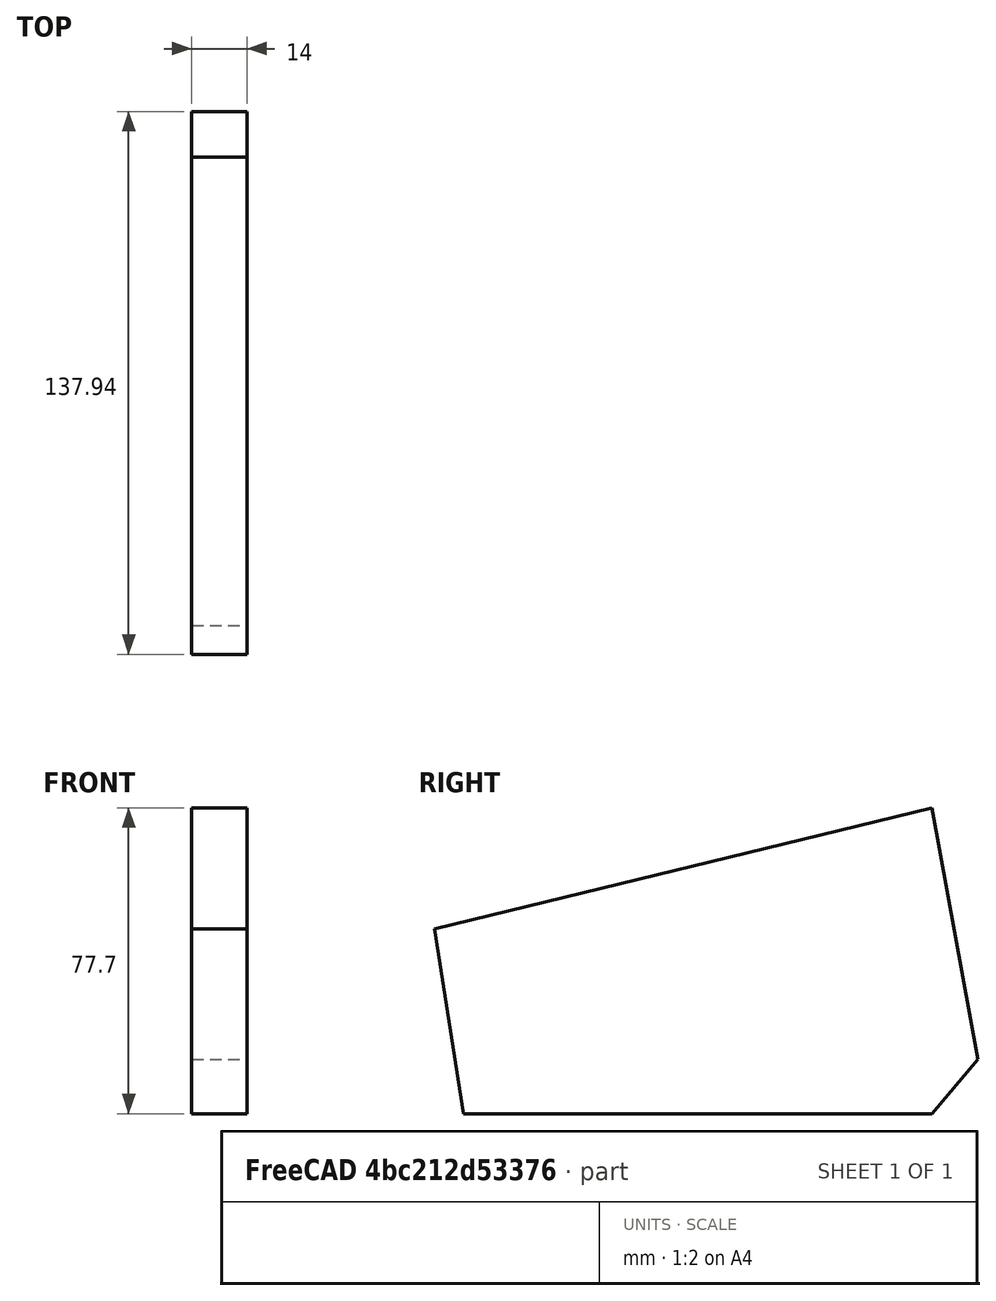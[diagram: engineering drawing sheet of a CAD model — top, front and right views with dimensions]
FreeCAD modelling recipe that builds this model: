
FCSTD DOCUMENT  (FreeCAD 1.0R39109 (Git))
Label: Griffschale Monitor-Controller Zeichnung
License: All rights reserved
objects: TechDraw::DrawViewDimension×13, TechDraw::DrawProjGroupItem×2, Sketcher::SketchObject×1, PartDesign::Pad×1, PartDesign::Body×1, TechDraw::DrawSVGTemplate×1, TechDraw::DrawProjGroup×1, TechDraw::DrawPage×1
note: 27 computed .brp shape members not serialized (recipe doc carries the construction recipe); baked Part::Feature solids carry a one-line shape summary decoded from their .brp

FEATURE [Sketcher::SketchObject] Sketch
  ArcFitTolerance = 1e-06
  AttachmentSupport = -> [YZ_Plane]
  FullyConstrained = true
  MakeInternals = false
  MapMode = 5
  Placement = pos=(0,0,0) rot=(0.57735,0.57735,0.57735;2.0944rad)
  sketch-geometry (9):
    g0: LineSegment StartX=7.32304 StartY=0 StartZ=0 EndX=126.323 EndY=0 EndZ=0
    g1: LineSegment StartX=126.323 StartY=0 StartZ=0 EndX=137.943 EndY=13.747 EndZ=0
    g2: LineSegment StartX=137.943 StartY=13.747 StartZ=0 EndX=126.323 EndY=77.7 EndZ=0
    g3: LineSegment StartX=126.323 StartY=77.7 StartZ=0 EndX=0 EndY=47 EndZ=0
    g4: LineSegment StartX=0 StartY=47 StartZ=0 EndX=7.32304 EndY=0 EndZ=0
    g5: LineSegment [constr] StartX=126.323 StartY=77.7 StartZ=0 EndX=-193.394 EndY=0 EndZ=0
    g6: LineSegment [constr] StartX=126.323 StartY=0 StartZ=0 EndX=-193.394 EndY=0 EndZ=0
    g7: LineSegment [constr] StartX=126.323 StartY=77.7 StartZ=0 EndX=126.323 EndY=0 EndZ=0
    g8: LineSegment [constr] StartX=0 StartY=47 StartZ=0 EndX=0 EndY=0 EndZ=0
  constraints (24):
    c: Coincident(g1,g2)
    c: Coincident(g3,g4)
    c: Coincident(g4,g0)
    c: Coincident(g5,g2)
    c: Horizontal(g6)
    c: Vertical(g7)
    c: Coincident(g8,g3)
    c: Vertical(g8)
    c: Coincident(g8,g-1)
    c: Horizontal(g0)
    c: PointOnObject(g3,g5)
    c: PointOnObject(g0,g-1)
    c: Coincident(g5,g6)
    c: Coincident(g7,g2)
    c: Coincident(g6,g1)
    c: Coincident(g1,g0)
    c: Coincident(g0,g7)
    c: Coincident(g2,g3)
    c: Distance(g3,g2) = 130
    c: DistanceX(g0,g0) = 119
    c: DistanceY(g7,g7) = 77.7
    c: DistanceY(g8,g8) = 47
    c: Distance(g2) = 65
    c: Distance(g1) = 18
FEATURE [PartDesign::Pad] Pad
  Direction = (1,0,0)
  Length = 14
  Length2 = 10
  Placement = pos=(0,0,0) rot=(1,1,1;2.0944rad)
  Profile = -> Sketch
  ReferenceAxis = -> Sketch [N_Axis]
  Refine = true
  Suppressed = false
  Type = 0
FEATURE [PartDesign::Body] Body  label="Körper"
  AllowCompound = false
  Group = -> [Sketch,Pad]
  Origin = -> Origin
  Tip = -> Pad
FEATURE [TechDraw::DrawSVGTemplate] Template  label="Vorlage"
  EditableTexts = approval_person=B. Hecate; creator=Andreas Schumm; date_of_issue=17.02.2025; document_type=Assembly Drawing; general_tolerances=ISO 2768-m; identification_number=DN; language_code=EN; legal_owner_1=crazy-midi.de; part_material=Holz; revision_index=AAA; sheet_number=1 / 1; sheet_scale=1 : 1; title=Griffschale
  Height = 210
  Orientation = 1
  Template = C:/Program Files/FreeCAD 1.0/data/Mod/TechDraw/Templates/A4_Landscape_ISO5457_minimal.svg
  Width = 297
FEATURE [TechDraw::DrawProjGroupItem] View  label="Front"
  CoarseView = false
  Direction = (0,0,1)
  Focus = 100
  HardHidden = false
  IsoCount = 0
  IsoHidden = false
  IsoVisible = false
  LockPosition = true
  Perspective = false
  Rotation = 0
  RotationVector = (1,0,0)
  ScaleType = 2
  ScrubCount = 1
  SeamHidden = false
  SeamVisible = false
  SmoothHidden = false
  SmoothVisible = true
  Source = -> [Body]
  Type = 0
  X = 0
  XDirection = (1e-16,-1,0)
  Y = 0
FEATURE [TechDraw::DrawViewDimension] Dimension010  label="Maß010"
  AngleOverride = false
  Arbitrary = false
  ArbitraryTolerances = false
  BoxCorners = (2) [(-92.1087,-7,0),(92.1087,7,0)]
  EqualTolerance = true
  ExtensionAngle = 0
  FormatSpec = %.2w
  FormatSpecOverTolerance = %+.2w
  FormatSpecUnderTolerance = %+.2w
  Inverted = false
  LineAngle = 0
  LockPosition = false
  MeasureType = 1
  OverTolerance = 0
  References2D = -> [View]
  Rotation = 0
  ScaleType = 0
  TheoreticalExact = false
  Type = 0
  UnderTolerance = 0
  X = -106.826
  Y = 0
FEATURE [TechDraw::DrawProjGroupItem] ProjItem  label="Untersicht"
  CoarseView = false
  Direction = (-1,-1e-16,0)
  Focus = 100
  HardHidden = false
  IsoCount = 0
  IsoHidden = false
  IsoVisible = false
  LockPosition = false
  Perspective = false
  Rotation = 0
  RotationVector = (1,0,0)
  ScaleType = 0
  ScrubCount = 1
  SeamHidden = false
  SeamVisible = false
  SmoothHidden = false
  SmoothVisible = true
  Source = -> [Body]
  Type = 5
  X = 0
  XDirection = (1e-16,-1,0)
  Y = 60.85
FEATURE [TechDraw::DrawProjGroup] ProjGroup
  Anchor = -> View
  AutoDistribute = true
  LockPosition = false
  ProjectionType = 0
  Rotation = 0
  ScaleType = 0
  Source = -> [Body]
  Views = -> [View,ProjItem]
  X = 154.736
  Y = 83.2975
  spacingX = 15
  spacingY = 15
FEATURE [TechDraw::DrawViewDimension] Dimension  label="Maß"
  AngleOverride = false
  Arbitrary = false
  ArbitraryTolerances = false
  BoxCorners = (2) [(-92.1087,-42.4554,0),(92.1087,42.4554,0)]
  EqualTolerance = true
  ExtensionAngle = 0
  FormatSpec = %.2w
  FormatSpecOverTolerance = %+.2w
  FormatSpecUnderTolerance = %+.2w
  Inverted = false
  LineAngle = 0
  LockPosition = false
  MeasureType = 1
  OverTolerance = 0
  References2D = -> [ProjItem]
  Rotation = 0
  ScaleType = 0
  TheoreticalExact = false
  Type = 0
  UnderTolerance = 0
  X = 7.25072
  Y = 23.3683
FEATURE [TechDraw::DrawViewDimension] Dimension008  label="Maß008"
  AngleOverride = false
  Arbitrary = false
  ArbitraryTolerances = false
  BoxCorners = (2) [(-92.1087,-42.4554,0),(92.1087,42.4554,0)]
  EqualTolerance = true
  ExtensionAngle = 0
  FormatSpec = %.2w
  FormatSpecOverTolerance = %+.2w
  FormatSpecUnderTolerance = %+.2w
  Inverted = false
  LineAngle = 0
  LockPosition = false
  MeasureType = 1
  OverTolerance = 0
  References2D = -> [ProjItem]
  Rotation = 0
  ScaleType = 0
  TheoreticalExact = false
  Type = 6
  UnderTolerance = 0
  X = -59.9984
  Y = -31.8576
FEATURE [TechDraw::DrawViewDimension] Dimension004  label="Maß004"
  AngleOverride = false
  Arbitrary = false
  ArbitraryTolerances = false
  BoxCorners = (2) [(-92.1087,-42.4554,0),(92.1087,42.4554,0)]
  EqualTolerance = true
  ExtensionAngle = 0
  FormatSpec = %.2w
  FormatSpecOverTolerance = %+.2w
  FormatSpecUnderTolerance = %+.2w
  Inverted = false
  LineAngle = 0
  LockPosition = false
  MeasureType = 1
  OverTolerance = 0
  References2D = -> [ProjItem]
  Rotation = 0
  ScaleType = 0
  TheoreticalExact = false
  Type = 0
  UnderTolerance = 0
  X = -89.9007
  Y = 10.4886
FEATURE [TechDraw::DrawViewDimension] Dimension003  label="Maß003"
  AngleOverride = false
  Arbitrary = false
  ArbitraryTolerances = false
  BoxCorners = (2) [(-92.1087,-42.4554,0),(92.1087,42.4554,0)]
  EqualTolerance = true
  ExtensionAngle = 0
  FormatSpec = %.2w
  FormatSpecOverTolerance = %+.2w
  FormatSpecUnderTolerance = %+.2w
  Inverted = false
  LineAngle = 0
  LockPosition = false
  MeasureType = 1
  OverTolerance = 0
  References2D = -> [ProjItem]
  Rotation = 0
  ScaleType = 0
  TheoreticalExact = false
  Type = 0
  UnderTolerance = 0
  X = -79.5706
  Y = -26.7398
FEATURE [TechDraw::DrawViewDimension] Dimension007  label="Maß007"
  AngleOverride = false
  Arbitrary = false
  ArbitraryTolerances = false
  BoxCorners = (2) [(-92.1087,-42.4554,0),(92.1087,42.4554,0)]
  EqualTolerance = true
  ExtensionAngle = 0
  FormatSpec = %.2w
  FormatSpecOverTolerance = %+.2w
  FormatSpecUnderTolerance = %+.2w
  Inverted = false
  LineAngle = 0
  LockPosition = false
  MeasureType = 1
  OverTolerance = 0
  References2D = -> [ProjItem]
  Rotation = 0
  ScaleType = 0
  TheoreticalExact = false
  Type = 0
  UnderTolerance = 0
  X = -1.75164
  Y = -32.7469
FEATURE [TechDraw::DrawViewDimension] Dimension005  label="Maß005"
  AngleOverride = false
  Arbitrary = false
  ArbitraryTolerances = false
  BoxCorners = (2) [(-92.1087,-42.4554,0),(92.1087,42.4554,0)]
  EqualTolerance = true
  ExtensionAngle = 0
  FormatSpec = %.2w
  FormatSpecOverTolerance = %+.2w
  FormatSpecUnderTolerance = %+.2w
  Inverted = false
  LineAngle = 0
  LockPosition = false
  MeasureType = 1
  OverTolerance = 0
  References2D = -> [ProjItem]
  Rotation = 0
  ScaleType = 0
  TheoreticalExact = false
  Type = 0
  UnderTolerance = 0
  X = 75.8826
  Y = -18.5645
FEATURE [TechDraw::DrawViewDimension] Dimension006  label="Maß006"
  AngleOverride = false
  Arbitrary = false
  ArbitraryTolerances = false
  BoxCorners = (2) [(-92.1087,-42.4554,0),(92.1087,42.4554,0)]
  EqualTolerance = true
  ExtensionAngle = 0
  FormatSpec = %.2w
  FormatSpecOverTolerance = %+.2w
  FormatSpecUnderTolerance = %+.2w
  Inverted = false
  LineAngle = 0
  LockPosition = false
  MeasureType = 1
  OverTolerance = 0
  References2D = -> [ProjItem]
  Rotation = 0
  ScaleType = 0
  TheoreticalExact = false
  Type = 6
  UnderTolerance = 0
  X = 64.9156
  Y = -9.62233
FEATURE [TechDraw::DrawViewDimension] Dimension009  label="Maß009"
  AngleOverride = false
  Arbitrary = false
  ArbitraryTolerances = false
  BoxCorners = (2) [(-92.1087,-42.4554,0),(92.1087,42.4554,0)]
  EqualTolerance = true
  ExtensionAngle = 0
  FormatSpec = %.2w
  FormatSpecOverTolerance = %+.2w
  FormatSpecUnderTolerance = %+.2w
  Inverted = false
  LineAngle = 0
  LockPosition = false
  MeasureType = 1
  OverTolerance = 0
  References2D = -> [ProjItem]
  Rotation = 0
  ScaleType = 0
  TheoreticalExact = false
  Type = 6
  UnderTolerance = 0
  X = -77.2108
  Y = -15.8925
FEATURE [TechDraw::DrawViewDimension] Dimension011  label="Maß011"
  AngleOverride = false
  Arbitrary = false
  ArbitraryTolerances = false
  BoxCorners = (2) [(-92.1087,-42.4554,0),(92.1087,42.4554,0)]
  EqualTolerance = true
  ExtensionAngle = 0
  FormatSpec = %.2w
  FormatSpecOverTolerance = %+.2w
  FormatSpecUnderTolerance = %+.2w
  Inverted = false
  LineAngle = 0
  LockPosition = false
  MeasureType = 1
  OverTolerance = 0
  References2D = -> [ProjItem]
  Rotation = 0
  ScaleType = 0
  TheoreticalExact = false
  Type = 2
  UnderTolerance = 0
  X = -123.308
  Y = 0
FEATURE [TechDraw::DrawViewDimension] Dimension013  label="Maß013"
  AngleOverride = false
  Arbitrary = false
  ArbitraryTolerances = false
  BoxCorners = (2) [(-92.1087,-7,0),(92.1087,7,0)]
  EqualTolerance = true
  ExtensionAngle = 0
  FormatSpec = %.2w
  FormatSpecOverTolerance = %+.2w
  FormatSpecUnderTolerance = %+.2w
  Inverted = false
  LineAngle = 0
  LockPosition = false
  MeasureType = 1
  OverTolerance = 0
  References2D = -> [View]
  Rotation = 0
  ScaleType = 0
  TheoreticalExact = false
  Type = 1
  UnderTolerance = 0
  X = 0
  Y = -20.0619
FEATURE [TechDraw::DrawViewDimension] Dimension014  label="Maß014"
  AngleOverride = false
  Arbitrary = false
  ArbitraryTolerances = false
  BoxCorners = (2) [(-92.1087,-42.4554,0),(92.1087,42.4554,0)]
  EqualTolerance = true
  ExtensionAngle = 0
  FormatSpec = %.2w
  FormatSpecOverTolerance = %+.2w
  FormatSpecUnderTolerance = %+.2w
  Inverted = false
  LineAngle = 0
  LockPosition = false
  MeasureType = 1
  OverTolerance = 0
  References2D = -> [ProjItem]
  Rotation = 0
  ScaleType = 0
  TheoreticalExact = false
  Type = 2
  UnderTolerance = 0
  X = 119.263
  Y = -13.0782
FEATURE [TechDraw::DrawViewDimension] Dimension015  label="Maß015"
  AngleOverride = false
  Arbitrary = false
  ArbitraryTolerances = false
  BoxCorners = (2) [(-92.1087,-42.4554,0),(92.1087,42.4554,0)]
  EqualTolerance = true
  ExtensionAngle = 0
  FormatSpec = %.2w
  FormatSpecOverTolerance = %+.2w
  FormatSpecUnderTolerance = %+.2w
  Inverted = false
  LineAngle = 0
  LockPosition = false
  MeasureType = 1
  OverTolerance = 0
  References2D = -> [ProjItem]
  Rotation = 0
  ScaleType = 0
  TheoreticalExact = false
  Type = 2
  UnderTolerance = 0
  X = -113.636
  Y = -29.68
FEATURE [TechDraw::DrawPage] Page  label="Seite"
  KeepUpdated = true
  NextBalloonIndex = 1
  ProjectionType = 0
  Template = -> Template
  Views = -> [ProjGroup,Dimension,Dimension003,Dimension004,Dimension005,Dimension006,Dimension007,Dimension008,Dimension009,Dimension010,Dimension011,Dimension013,Dimension014,Dimension015]
